# Revit family: Gleiter GL-100 o. Lasche, 1xAG
name_source: partatom
category: HLS-Bauteile
revit_build: Autodesk Revit 2017 (Build: 20190507_1515(x64)
units: mm (PartAtom-declared; Revit-internal decimal feet)

## family parameters
Arbeitsebenenbasiert = Ja
Beim Laden mit Abzugskörper schneiden = Nein
Bemaßung runder Anschluss = Durchmesser verwenden
Gemeinsam genutzt = Ja
Immer vertikal = Nein
Raumberechnungspunkt = Nein
Teiletyp = Normal

## types (4) — shared parameters
Anzahl Anschlüsse = 1
Ausführung = ohne Lasche
B = 160 mm  [stored 0.524934 ft]
B1 = 58 mm  [stored 0.190289 ft]
Breite = 67 mm
Fabrikat = MEFA
Firma = MEFA Befestigungs- und Montagesysteme GmbH
Gleitreibungsfaktor = 0.15 - 0.25
H1 = 15 mm  [stored 0.0492126 ft]
Haftreibungsfaktor = 0,2 - 0,3
Kurztext1 = Gleiter axial GL 100
L1 = 80 mm  [stored 0.262467 ft]
Lochdurchmesser = 13 mm
Länge = 160 mm  [stored 0.524934 ft]
MD = 3 mm  [stored 0.00984252 ft]
Material Gleitelement = Stahl
Material Gleitstreifen = Kunststoff
Materialname Gleitelement = S235JR
Materialname Gleitstreifen = Polyamid 6
Mengeneinheit = St
Vorgabe-Ansicht = 1219 mm
max. Schiebeweg axial = 75 mm
max. Temperaturbeständigkeit = 100 °C

## per-type parameters (varying)
| type | Anschluss | Anschlussgewinde | Artikelnummer | Bauhöhe | EAN | Gewicht | Gewicht pro Bauteil | Gewinde | H | Kurztext2 | vpe |
| Gleiter GL-100, M10 | 1 x M10 | 6kt-Mutter parametrik : Hutmutter gedreht M10 (4130010) | 0770524 | 35 mm | 4250928417862 | 0.52 kg | 0.52 kg | M10 | 35 mm  [stored 0.114829 ft] | Anschluss 1 x M10 ohne Lasche | 20 St |
| Gleiter GL-100, M12 | 1 x M12 | 6kt-Mutter parametrik : Hutmutter gedreht M12 (4130012) | 0770532 | 37 mm | 4250928417923 | 0.53 kg | 0.53 kg | M12 | 37 mm  [stored 0.121391 ft] | Anschluss 1 x M12 ohne Lasche | 20 St |
| Gleiter GL-100, M16 | 1 x M16 | 6kt-Mutter parametrik : Hutmutter M16 (4130016) | 0770559 | 36 mm | 4250928418036 | 0.54 kg | 0.54 kg | M16 | 36 mm  [stored 0.11811 ft] | Anschluss 1 x M16 ohne Lasche | 1 St |
| Gleiter GL-100, 1/2" | 1 x 1/2'' | Runde Gewindeanschlusse parametrik : Muffe 1/2´´ (0009865) | 0770605 | 36 mm | 4250928418104 | 0.53 kg | 0.53 kg | 1/2'' | 36 mm  [stored 0.11811 ft] | Anschluss 1 x 1/2'' ohne Lasche | 1 St |

note: [stored X ft] marks values corroborated as IEEE doubles in the binary element streams (Revit-internal decimal feet)

## geometry (parser evidence)
native form markers: Sweep x1
no freeform markers — native parametric forms only
